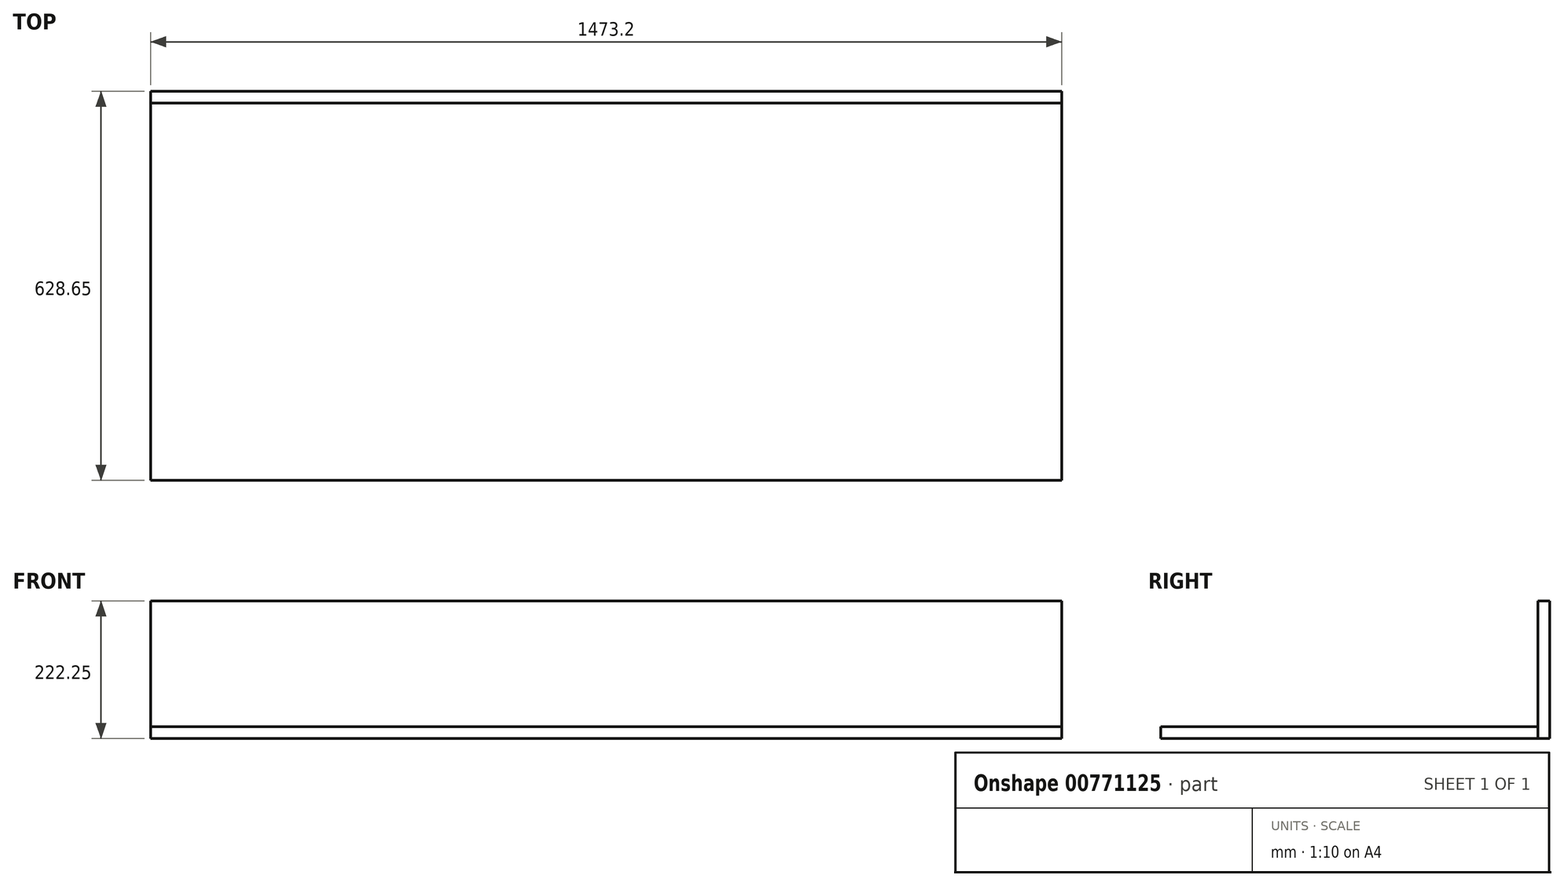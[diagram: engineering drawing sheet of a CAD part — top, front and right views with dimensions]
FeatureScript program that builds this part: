
annotation { "Feature Type Name" : "Feature", "Feature Type Description" : "" }
export const myFeature = defineFeature(function(context is Context, id is Id, definition is map)
    precondition{}
    {
        {
            var Q0;
            Q0=qCreatedBy(makeId("Right.planeOp"),FACE);
            var sketch = newSketch(context, id + "F0", { "sketchPlane" : qUnion([Q0])});
            skLineSegment(sketch, "E0.bottom", {"start": v(0, 0) * mm, "end": v(-609.6, 0) * mm});
            skLineSegment(sketch, "E0.top", {"start": v(0, 19.05) * mm, "end": v(-609.6, 19.05) * mm});
            skLineSegment(sketch, "E0.left", {"start": v(0, 0) * mm, "end": v(0, 19.05) * mm});
            skLineSegment(sketch, "E0.right", {"start": v(-609.6, 0) * mm, "end": v(-609.6, 19.05) * mm});
            skSolve(sketch);
        }
        {
            var Q0;
            Q0 = qSketchRegion(id + "F0", true);
            extrude(context, id + "F1", {"entities" : qUnion([Q0]), "endBound" : BoundingType.SYMMETRIC, "depth" : 1473.2 * mm, "offsetDistance" : 25.4 * mm});
        }
        {
            var Q0;
            Q0=qCreatedBy(makeId("Top.planeOp"),FACE);
            var sketch = newSketch(context, id + "F2", { "sketchPlane" : qUnion([Q0])});
            skLineSegment(sketch, "E1.bottom", {"start": v(736.6, 0) * mm, "end": v(-736.6, 0) * mm});
            skLineSegment(sketch, "E1.top", {"start": v(736.6, 19.05) * mm, "end": v(-736.6, 19.05) * mm});
            skLineSegment(sketch, "E1.left", {"start": v(736.6, 0) * mm, "end": v(736.6, 19.05) * mm});
            skLineSegment(sketch, "E1.right", {"start": v(-736.6, 0) * mm, "end": v(-736.6, 19.05) * mm});
            skSolve(sketch);
        }
        {
            var Q0;
            Q0 = qSketchRegion(id + "F2", true);
            extrude(context, id + "F3", {"entities" : qUnion([Q0]), "depth" : 222.25 * mm, "offsetDistance" : 25.4 * mm});
        }
    });
